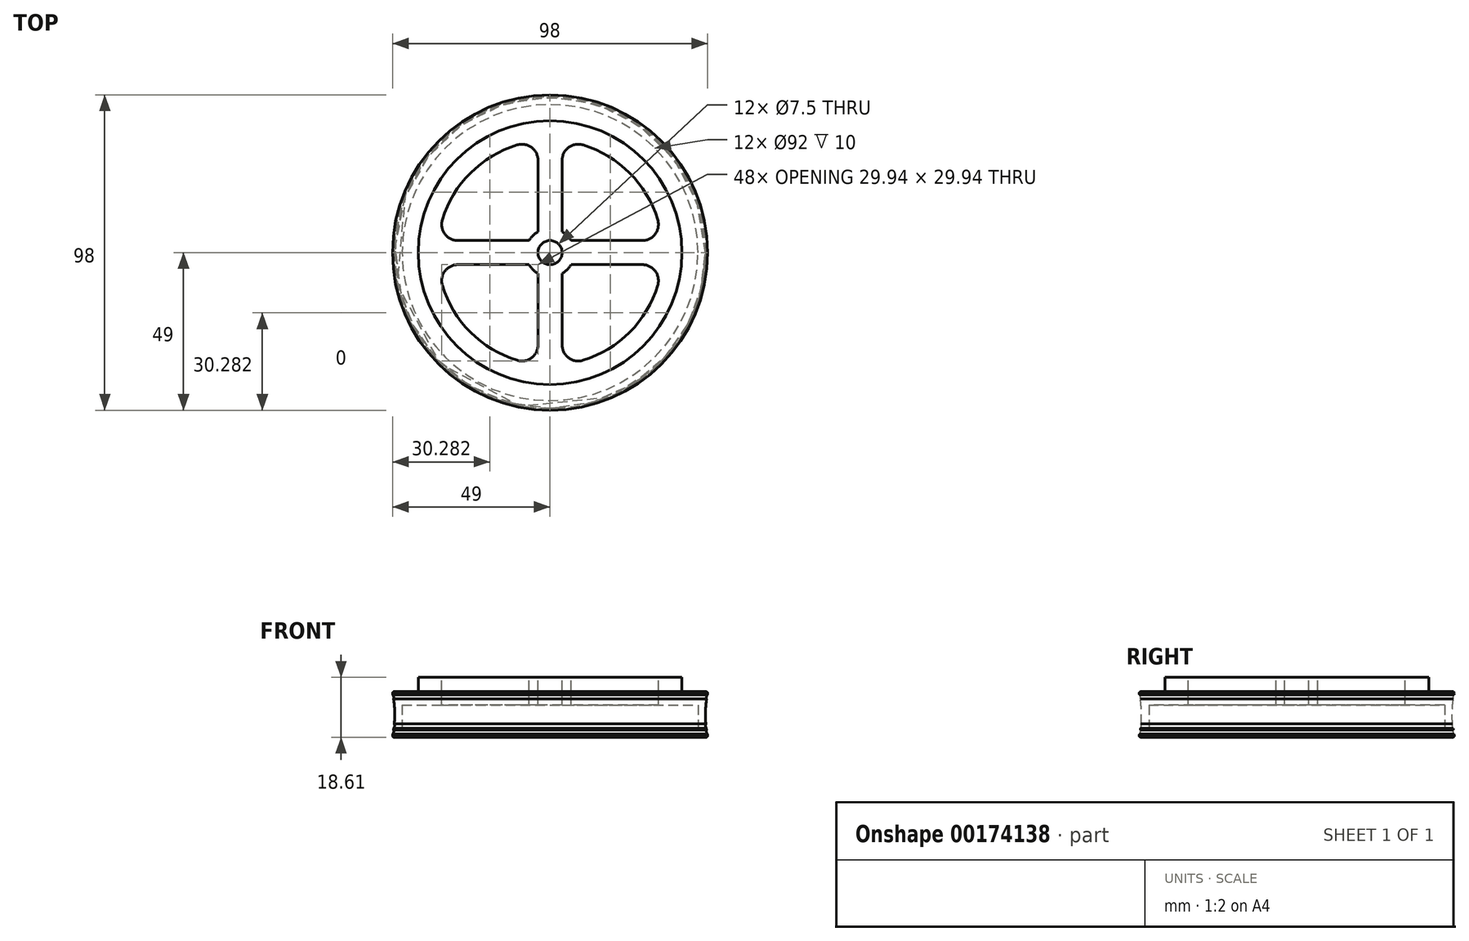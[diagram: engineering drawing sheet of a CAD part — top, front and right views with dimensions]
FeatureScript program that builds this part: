
annotation { "Feature Type Name" : "Feature", "Feature Type Description" : "" }
export const myFeature = defineFeature(function(context is Context, id is Id, definition is map)
    precondition{}
    {
        {
            var Q0;
            Q0=qCreatedBy(makeId("Front.planeOp"),FACE);
            var sketch = newSketch(context, id + "F4", { "sketchPlane" : qUnion([Q0])});
            skLineSegment(sketch, "E0", {"start": v(0, -14.16) * mm, "end": v(48.5, -14.16) * mm});
            skLineSegment(sketch, "E1", {"start": v(48.5, 0) * mm, "end": v(41, 0) * mm});
            skLineSegment(sketch, "E2", {"start": v(41, 0) * mm, "end": v(41, 4.45) * mm});
            skLineSegment(sketch, "E3", {"start": v(41, 4.45) * mm, "end": v(0, 4.45) * mm});
            skLineSegment(sketch, "E4", {"start": v(0, 4.45) * mm, "end": v(0, -14.16) * mm});
            skPoint(sketch, "E5.visualSharp", {"position": v(49, -14.16) * mm});
            skArc(sketch, "E5.filletArc", {"start": v(48.5, -14.16) * mm, "mid": v(48.85, -14.02) * mm, "end": v(49, -13.66) * mm});
            skPoint(sketch, "E6.visualSharp", {"position": v(49, 0) * mm});
            skArc(sketch, "E6.filletArc", {"start": v(49, -0.5) * mm, "mid": v(48.85, -0.15) * mm, "end": v(48.5, 0) * mm});
            skArc(sketch, "E7", {"start": v(49, -0.5) * mm, "mid": v(48.95, -0.74) * mm, "end": v(48.9, -0.99) * mm});
            skArc(sketch, "E8", {"start": v(48.67, -11.86) * mm, "mid": v(48.63, -12.54) * mm, "end": v(48.9, -13.17) * mm});
            skArc(sketch, "E9.trimOffspring", {"start": v(48.9, -13.17) * mm, "mid": v(48.95, -13.42) * mm, "end": v(49, -13.66) * mm});
            skArc(sketch, "E10", {"start": v(48.45, -10.03) * mm, "mid": v(48.37, -10.71) * mm, "end": v(48.6, -11.36) * mm});
            skArc(sketch, "E11.trimOffspring", {"start": v(48.6, -11.36) * mm, "mid": v(48.63, -11.6) * mm, "end": v(48.67, -11.86) * mm});
            skArc(sketch, "E12", {"start": v(48.9, -0.99) * mm, "mid": v(48.63, -1.62) * mm, "end": v(48.67, -2.3) * mm});
            skArc(sketch, "E13.trimOffspring", {"start": v(48.67, -2.3) * mm, "mid": v(48.32, -6.16) * mm, "end": v(48.45, -10.03) * mm});
            skSolve(sketch);
        }
        {
            var Q0;
            Q0=makeQuery(id+"F4.imprint","IMPRINT",FACE,{"disambiguationData":[TD([[makeQuery(id+"F4.imprint","IMPRINT",EDGE,{"derivedFrom":sQuery(id+"F4.wireOp",EDGE,"E0")}),1.0]])]});
            var Q1;
            Q1=sQuery(id+"F4.wireOp",EDGE,"E4");
            revolve(context, id + "F5", {"entities" : qUnion([Q0]), "axis" : qUnion([Q1]), "revolveType" : RevolveType.FULL});
        }
        {
            var Q0;
            Q0=makeQuery(id+"F5.opRevolve","SWEPT_FACE",FACE,{"disambiguationData":[OSD([sQuery(id+"F4.wireOp",EDGE,"E3")])]});
            var sketch = newSketch(context, id + "F0", { "sketchPlane" : qUnion([Q0])});
            skCircle(sketch, "E14.0", {"center": v(0, 0) * mm, "radius": 41 * mm});
            skArc(sketch, "E15", {"start": v(-10.2, 33.48) * mm, "mid": v(-24.75, 24.75) * mm, "end": v(-33.48, 10.2) * mm});
            skLineSegment(sketch, "E16.left", {"start": v(3.75, 28.7) * mm, "end": v(3.75, 6.5) * mm});
            skLineSegment(sketch, "E16.right", {"start": v(-3.75, 28.7) * mm, "end": v(-3.75, 6.5) * mm});
            skLineSegment(sketch, "E17.bottom", {"start": v(28.7, 3.75) * mm, "end": v(6.5, 3.75) * mm});
            skLineSegment(sketch, "E17.top", {"start": v(28.7, -3.75) * mm, "end": v(6.5, -3.75) * mm});
            skArc(sketch, "E18", {"start": v(6.5, 3.75) * mm, "mid": v(5.3, 5.3) * mm, "end": v(3.75, 6.5) * mm});
            skLineSegment(sketch, "E19.trimOffspring", {"start": v(-6.5, 3.75) * mm, "end": v(-28.7, 3.75) * mm});
            skLineSegment(sketch, "E20.trimOffspring", {"start": v(-3.75, -6.5) * mm, "end": v(-3.75, -28.7) * mm});
            skLineSegment(sketch, "E21.trimOffspring", {"start": v(3.75, -6.5) * mm, "end": v(3.75, -28.7) * mm});
            skLineSegment(sketch, "E22.trimOffspring", {"start": v(-6.5, -3.75) * mm, "end": v(-28.7, -3.75) * mm});
            skArc(sketch, "E23.trimOffspring", {"start": v(-3.75, 6.5) * mm, "mid": v(-5.3, 5.3) * mm, "end": v(-6.5, 3.75) * mm});
            skArc(sketch, "E24.trimOffspring", {"start": v(-6.5, -3.75) * mm, "mid": v(-5.3, -5.3) * mm, "end": v(-3.75, -6.5) * mm});
            skArc(sketch, "E25.trimOffspring", {"start": v(3.75, -6.5) * mm, "mid": v(5.3, -5.3) * mm, "end": v(6.5, -3.75) * mm});
            skArc(sketch, "E26.trimOffspring", {"start": v(-33.48, -10.2) * mm, "mid": v(-24.75, -24.75) * mm, "end": v(-10.2, -33.48) * mm});
            skArc(sketch, "E27.trimOffspring", {"start": v(10.2, -33.48) * mm, "mid": v(24.75, -24.75) * mm, "end": v(33.48, -10.2) * mm});
            skArc(sketch, "E28.trimOffspring", {"start": v(33.48, 10.2) * mm, "mid": v(24.75, 24.75) * mm, "end": v(10.2, 33.48) * mm});
            skPoint(sketch, "E29.visualSharp", {"position": v(-3.75, 34.8) * mm});
            skArc(sketch, "E29.filletArc", {"start": v(-3.75, 28.7) * mm, "mid": v(-5.77, 32.71) * mm, "end": v(-10.2, 33.48) * mm});
            skPoint(sketch, "E30.visualSharp", {"position": v(-34.8, 3.75) * mm});
            skArc(sketch, "E30.filletArc", {"start": v(-33.48, 10.2) * mm, "mid": v(-32.71, 5.77) * mm, "end": v(-28.7, 3.75) * mm});
            skPoint(sketch, "E31.visualSharp", {"position": v(-34.8, -3.75) * mm});
            skArc(sketch, "E31.filletArc", {"start": v(-28.7, -3.75) * mm, "mid": v(-32.71, -5.77) * mm, "end": v(-33.48, -10.2) * mm});
            skPoint(sketch, "E32.visualSharp", {"position": v(-3.75, -34.8) * mm});
            skArc(sketch, "E32.filletArc", {"start": v(-10.2, -33.48) * mm, "mid": v(-5.77, -32.71) * mm, "end": v(-3.75, -28.7) * mm});
            skPoint(sketch, "E33.visualSharp", {"position": v(3.75, -34.8) * mm});
            skArc(sketch, "E33.filletArc", {"start": v(3.75, -28.7) * mm, "mid": v(5.77, -32.71) * mm, "end": v(10.2, -33.48) * mm});
            skPoint(sketch, "E34.visualSharp", {"position": v(34.8, -3.75) * mm});
            skArc(sketch, "E34.filletArc", {"start": v(33.48, -10.2) * mm, "mid": v(32.71, -5.77) * mm, "end": v(28.7, -3.75) * mm});
            skPoint(sketch, "E35.visualSharp", {"position": v(34.8, 3.75) * mm});
            skArc(sketch, "E35.filletArc", {"start": v(28.7, 3.75) * mm, "mid": v(32.71, 5.77) * mm, "end": v(33.48, 10.2) * mm});
            skPoint(sketch, "E36.visualSharp", {"position": v(3.75, 34.8) * mm});
            skArc(sketch, "E36.filletArc", {"start": v(10.2, 33.48) * mm, "mid": v(5.77, 32.71) * mm, "end": v(3.75, 28.7) * mm});
            skCircle(sketch, "E37", {"center": v(0, 0) * mm, "radius": 3.75 * mm});
            skSolve(sketch);
        }
        {
            var Q0;
            Q0=sQuery(id+"F0.wireOp",VERTEX,"E14.0.center");
            var Q1;
            Q1=makeQuery(id+"F5.opRevolve","SWEPT_BODY",BODY,{"disambiguationData":[OSD([sQuery(id+"F4.wireOp",EDGE,"E0"),sQuery(id+"F4.wireOp",EDGE,"E1"),sQuery(id+"F4.wireOp",EDGE,"E2"),sQuery(id+"F4.wireOp",EDGE,"E3"),sQuery(id+"F4.wireOp",EDGE,"E4"),sQuery(id+"F4.wireOp",EDGE,"E5.filletArc"),sQuery(id+"F4.wireOp",EDGE,"E6.filletArc"),sQuery(id+"F4.wireOp",EDGE,"E7"),sQuery(id+"F4.wireOp",EDGE,"E8"),sQuery(id+"F4.wireOp",EDGE,"E9.trimOffspring"),sQuery(id+"F4.wireOp",EDGE,"E10"),sQuery(id+"F4.wireOp",EDGE,"E11.trimOffspring"),sQuery(id+"F4.wireOp",EDGE,"E12"),sQuery(id+"F4.wireOp",EDGE,"E13.trimOffspring")])]});
            hole(context, id + "F1", {"style" : HoleStyle.SIMPLE, "endStyle" : HoleEndStyle.THROUGH, "holeDiameter" : 7.5 * mm, "locations" : qUnion([Q0]), "scope" : qUnion([Q1]), "isTappedThrough" : true});
        }
        {
            var Q0;
            Q0=makeQuery(id+"F0.imprint","IMPRINT",FACE,{"disambiguationData":[TD([[makeQuery(id+"F0.imprint","IMPRINT",EDGE,{"derivedFrom":sQuery(id+"F0.wireOp",EDGE,"E15")}),1.0]])]});
            var Q1;
            Q1=makeQuery(id+"F0.imprint","IMPRINT",FACE,{"disambiguationData":[TD([[makeQuery(id+"F0.imprint","IMPRINT",EDGE,{"derivedFrom":sQuery(id+"F0.wireOp",EDGE,"E20.trimOffspring")}),-1.0]])]});
            var Q2;
            Q2=makeQuery(id+"F0.imprint","IMPRINT",FACE,{"disambiguationData":[TD([[makeQuery(id+"F0.imprint","IMPRINT",EDGE,{"derivedFrom":sQuery(id+"F0.wireOp",EDGE,"E17.top")}),1.0]])]});
            var Q3;
            Q3=makeQuery(id+"F0.imprint","IMPRINT",FACE,{"disambiguationData":[TD([[makeQuery(id+"F0.imprint","IMPRINT",EDGE,{"derivedFrom":sQuery(id+"F0.wireOp",EDGE,"E16.left")}),1.0]])]});
            extrude(context, id + "F6", {"entities" : qUnion([Q0, Q1, Q2, Q3]), "operationType" : NewBodyOperationType.REMOVE, "oppositeDirection" : true, "depth" : 56.02 * mm});
        }
        {
            var Q0;
            Q0=makeQuery(id+"F5.opRevolve","SWEPT_FACE",FACE,{"disambiguationData":[OSD([sQuery(id+"F4.wireOp",EDGE,"E0")])]});
            var sketch = newSketch(context, id + "F7", { "sketchPlane" : qUnion([Q0])});
            skCircle(sketch, "E38.0", {"center": v(0, 0) * mm, "radius": 48.5 * mm});
            skCircle(sketch, "E39", {"center": v(0, 0) * mm, "radius": 46 * mm});
            skSolve(sketch);
        }
        {
            var Q0;
            Q0=makeQuery(id+"F7.imprint","IMPRINT",FACE,{"disambiguationData":[TD([[makeQuery(id+"F7.imprint","IMPRINT",EDGE,{"derivedFrom":sQuery(id+"F7.wireOp",EDGE,"E39")}),1.0]])]});
            extrude(context, id + "F2", {"entities" : qUnion([Q0]), "operationType" : NewBodyOperationType.REMOVE, "oppositeDirection" : true, "depth" : 10 * mm});
        }
    });
